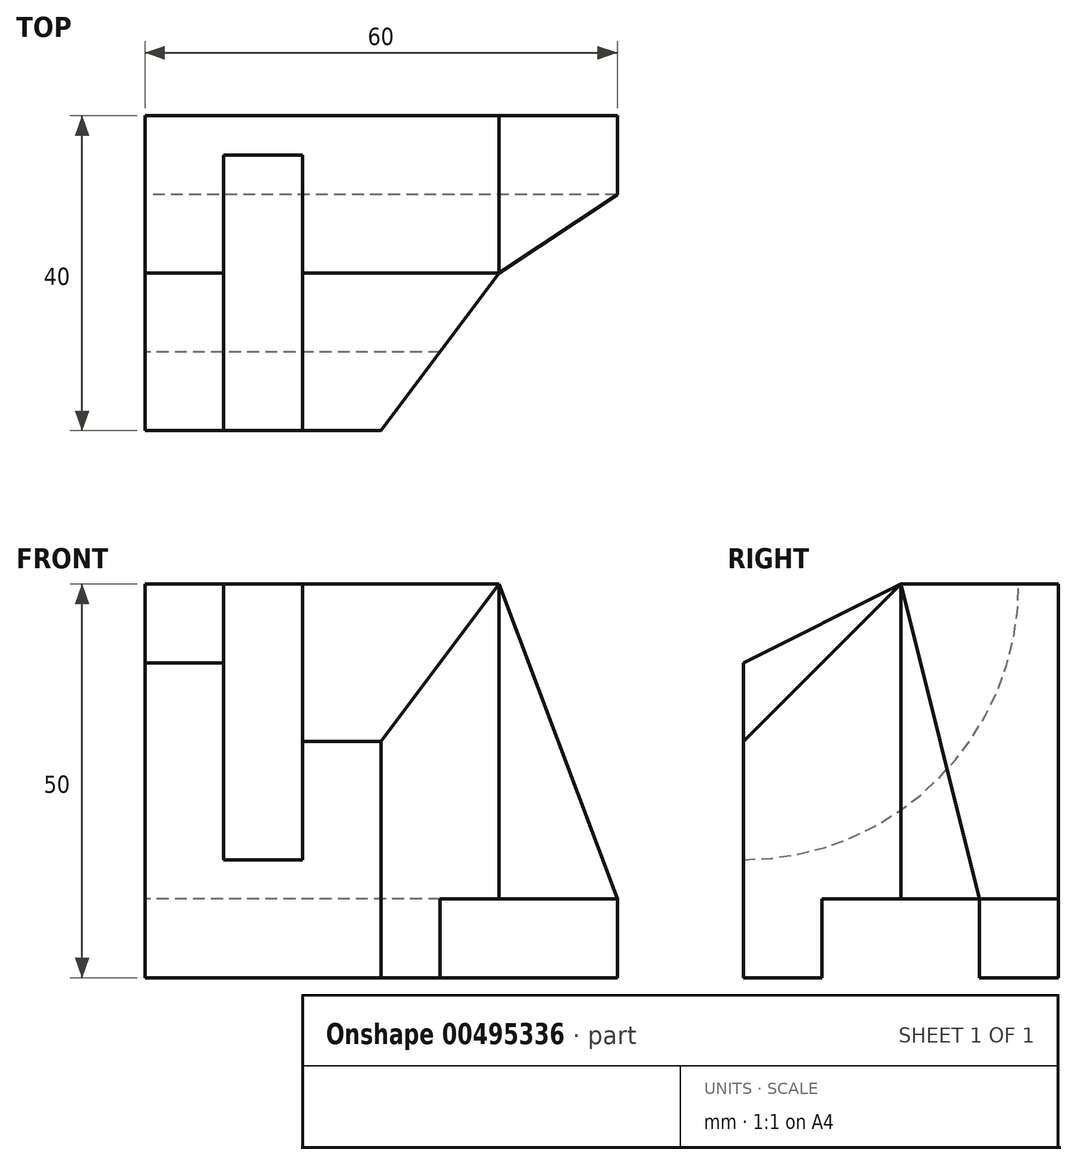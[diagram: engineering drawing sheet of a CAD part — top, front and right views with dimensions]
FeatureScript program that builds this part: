
annotation { "Feature Type Name" : "Feature", "Feature Type Description" : "" }
export const myFeature = defineFeature(function(context is Context, id is Id, definition is map)
    precondition{}
    {
        {
            var Q0;
            Q0=qCreatedBy(makeId("Top.planeOp"),FACE);
            var sketch = newSketch(context, id + "F0", { "sketchPlane" : qUnion([Q0])});
            skLineSegment(sketch, "E0.bottom", {"start": v(0, 0) * mm, "end": v(60, 0) * mm});
            skLineSegment(sketch, "E0.top", {"start": v(0, -40) * mm, "end": v(60, -40) * mm});
            skLineSegment(sketch, "E0.left", {"start": v(0, 0) * mm, "end": v(0, -40) * mm});
            skLineSegment(sketch, "E0.right", {"start": v(60, 0) * mm, "end": v(60, -40) * mm});
            skSolve(sketch);
        }
        {
            var Q0;
            Q0 = qSketchRegion(id + "F0", true);
            extrude(context, id + "F1", {"entities" : qUnion([Q0]), "depth" : 50 * mm});
        }
        {
            var Q0;
            Q0=makeQuery(id+"F1.opExtrude","SWEPT_FACE",FACE,{"disambiguationData":[OSD([sQuery(id+"F0.wireOp",EDGE,"E0.left")])]});
            var sketch = newSketch(context, id + "F2", { "sketchPlane" : qUnion([Q0])});
            skLineSegment(sketch, "E1", {"start": v(20, 50) * mm, "end": v(40, 40) * mm});
            skLineSegment(sketch, "E2", {"start": v(40, 40) * mm, "end": v(40, 50) * mm});
            skLineSegment(sketch, "E3", {"start": v(40, 50) * mm, "end": v(20, 50) * mm});
            skSolve(sketch);
        }
        {
            var Q0;
            Q0=makeQuery(id+"F1.opExtrude","CAP_FACE",FACE,{"disambiguationData":[OSD([sQuery(id+"F0.wireOp",EDGE,"E0.bottom"),sQuery(id+"F0.wireOp",EDGE,"E0.top"),sQuery(id+"F0.wireOp",EDGE,"E0.left"),sQuery(id+"F0.wireOp",EDGE,"E0.right")])],"isStart":false});
            var sketch = newSketch(context, id + "F3", { "sketchPlane" : qUnion([Q0])});
            skLineSegment(sketch, "E4.bottom", {"start": v(10, -40) * mm, "end": v(20, -40) * mm});
            skLineSegment(sketch, "E4.top", {"start": v(10, -5) * mm, "end": v(20, -5) * mm});
            skLineSegment(sketch, "E4.left", {"start": v(10, -40) * mm, "end": v(10, -5) * mm});
            skLineSegment(sketch, "E4.right", {"start": v(20, -40) * mm, "end": v(20, -5) * mm});
            skLineSegment(sketch, "E5", {"start": v(30, -40) * mm, "end": v(45, -20) * mm});
            skLineSegment(sketch, "E6", {"start": v(45, -20) * mm, "end": v(60, -10) * mm});
            skLineSegment(sketch, "E7", {"start": v(60, -10) * mm, "end": v(60, -40) * mm});
            skLineSegment(sketch, "E8", {"start": v(60, -40) * mm, "end": v(30, -40) * mm});
            skSolve(sketch);
        }
        {
            var Q0;
            Q0=makeQuery(id+"F1.opExtrude","CAP_FACE",FACE,{"disambiguationData":[OSD([sQuery(id+"F0.wireOp",EDGE,"E0.bottom"),sQuery(id+"F0.wireOp",EDGE,"E0.top"),sQuery(id+"F0.wireOp",EDGE,"E0.left"),sQuery(id+"F0.wireOp",EDGE,"E0.right")])],"isStart":true});
            cPlane(context, id + "F4", {"entities" : qUnion([Q0]), "cplaneType" : CPlaneType.OFFSET, "offset" : 15 * mm, "oppositeDirection" : true, "width" : 150 * mm, "height" : 150 * mm});
        }
        {
            var Q0;
            Q0=makeQuery(id+"F3.imprint","IMPRINT",FACE,{"disambiguationData":[TD([[makeQuery(id+"F3.imprint","IMPRINT",EDGE,{"derivedFrom":sQuery(id+"F3.wireOp",EDGE,"E4.bottom")}),1.0]])]});
            var Q1;
            Q1=qCreatedBy(id+"F4.planeOp",FACE);
            extrude(context, id + "F5", {"entities" : qUnion([Q0]), "operationType" : NewBodyOperationType.REMOVE, "endBound" : BoundingType.UP_TO_SURFACE, "oppositeDirection" : true, "endBoundEntityFace" : qUnion([Q1]), "depth" : 25 * mm});
        }
        {
            var Q0;
            Q0=makeQuery(id+"F5.boolean.opBoolean","COPY",EDGE,{"derivedFrom":makeQuery(id+"F5.opExtrude","CAP_EDGE",EDGE,{"disambiguationData":[OSD([sQuery(id+"F3.wireOp",EDGE,"E4.top")])],"isStart":false})});
            fillet(context, id + "F6", {"entities" : qUnion([Q0]), "radius" : 35 * mm, "tangentPropagation" : true, "allowEdgeOverflow" : false});
        }
        {
            var Q0;
            Q0=makeQuery(id+"F2.imprint","IMPRINT",FACE,{"disambiguationData":[TD([[makeQuery(id+"F2.imprint","IMPRINT",EDGE,{"derivedFrom":sQuery(id+"F2.wireOp",EDGE,"E1")}),1.0]])]});
            extrude(context, id + "F7", {"entities" : qUnion([Q0]), "operationType" : NewBodyOperationType.REMOVE, "oppositeDirection" : true, "depth" : 12.7 * mm});
        }
        {
            var Q0;
            Q0=makeQuery(id+"F1.opExtrude","SWEPT_FACE",FACE,{"disambiguationData":[OSD([sQuery(id+"F0.wireOp",EDGE,"E0.right")])]});
            var sketch = newSketch(context, id + "F8", { "sketchPlane" : qUnion([Q0])});
            skLineSegment(sketch, "E9", {"start": v(-20, 50) * mm, "end": v(-40, 30) * mm});
            skLineSegment(sketch, "E10", {"start": v(-40, 30) * mm, "end": v(-40, 50) * mm});
            skLineSegment(sketch, "E11", {"start": v(-40, 50) * mm, "end": v(-20, 50) * mm});
            skSolve(sketch);
        }
        {
            var Q0;
            Q0 = qSketchRegion(id + "F8", true);
            extrude(context, id + "F9", {"entities" : qUnion([Q0]), "operationType" : NewBodyOperationType.REMOVE, "endBound" : BoundingType.UP_TO_NEXT, "oppositeDirection" : true, "depth" : 25 * mm});
        }
        {
            var Q0;
            Q0=makeQuery(id+"F3.imprint","IMPRINT",FACE,{"disambiguationData":[TD([[makeQuery(id+"F3.imprint","IMPRINT",EDGE,{"derivedFrom":sQuery(id+"F3.wireOp",EDGE,"E5")}),-1.0]])]});
            extrude(context, id + "F10", {"entities" : qUnion([Q0]), "operationType" : NewBodyOperationType.REMOVE, "endBound" : BoundingType.THROUGH_ALL, "oppositeDirection" : true, "depth" : 25 * mm});
        }
        {
            var Q0;
            Q0=makeQuery(id+"F1.opExtrude","SWEPT_FACE",FACE,{"disambiguationData":[OSD([sQuery(id+"F0.wireOp",EDGE,"E0.bottom")])]});
            var sketch = newSketch(context, id + "F11", { "sketchPlane" : qUnion([Q0])});
            skLineSegment(sketch, "E12", {"start": v(-45, 50) * mm, "end": v(-60, 50) * mm});
            skLineSegment(sketch, "E13", {"start": v(-60, 50) * mm, "end": v(-60, 10) * mm});
            skLineSegment(sketch, "E14", {"start": v(-60, 10) * mm, "end": v(-45, 50) * mm});
            skSolve(sketch);
        }
        {
            var Q0;
            Q0 = qSketchRegion(id + "F11", true);
            extrude(context, id + "F12", {"entities" : qUnion([Q0]), "operationType" : NewBodyOperationType.REMOVE, "endBound" : BoundingType.UP_TO_NEXT, "oppositeDirection" : true, "depth" : 25 * mm});
        }
        {
            var Q0;
            Q0=makeQuery(id+"F1.opExtrude","SWEPT_FACE",FACE,{"disambiguationData":[OSD([sQuery(id+"F0.wireOp",EDGE,"E0.left")])]});
            var sketch = newSketch(context, id + "F13", { "sketchPlane" : qUnion([Q0])});
            skLineSegment(sketch, "E15.bottom", {"start": v(30, 0) * mm, "end": v(10, 0) * mm});
            skLineSegment(sketch, "E15.top", {"start": v(30, 10) * mm, "end": v(10, 10) * mm});
            skLineSegment(sketch, "E15.left", {"start": v(30, 0) * mm, "end": v(30, 10) * mm});
            skLineSegment(sketch, "E15.right", {"start": v(10, 0) * mm, "end": v(10, 10) * mm});
            skSolve(sketch);
        }
        {
            var Q0;
            Q0 = qSketchRegion(id + "F13", true);
            extrude(context, id + "F14", {"entities" : qUnion([Q0]), "operationType" : NewBodyOperationType.REMOVE, "endBound" : BoundingType.THROUGH_ALL, "oppositeDirection" : true, "depth" : 25 * mm});
        }
    });
